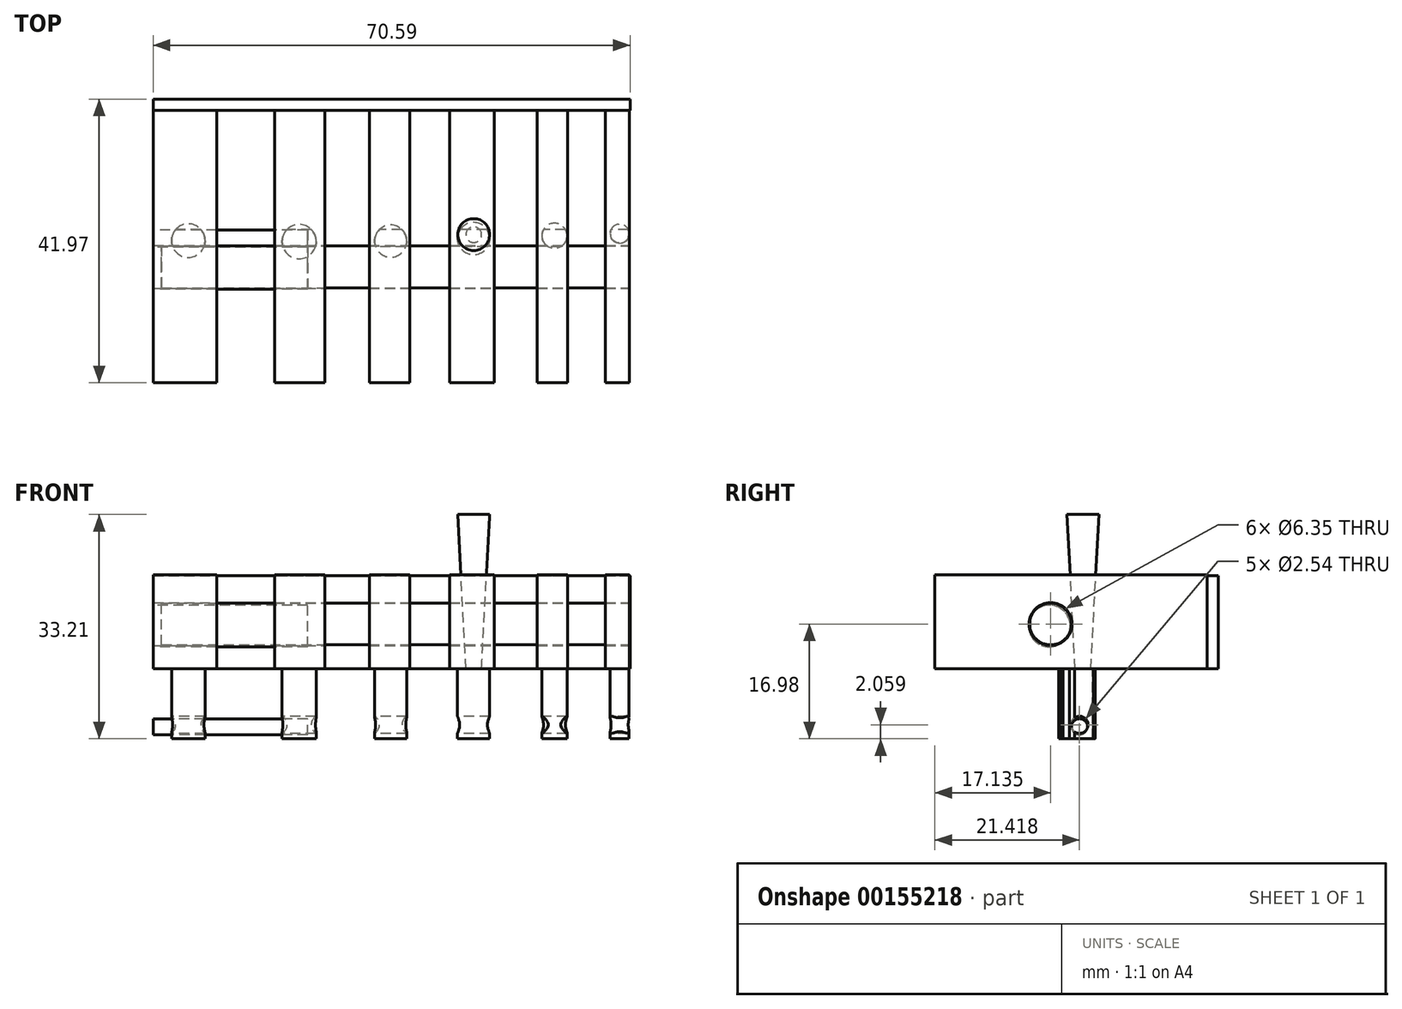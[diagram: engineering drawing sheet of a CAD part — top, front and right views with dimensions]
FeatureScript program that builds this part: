
annotation { "Feature Type Name" : "Feature", "Feature Type Description" : "" }
export const myFeature = defineFeature(function(context is Context, id is Id, definition is map)
    precondition{}
    {
        {
            var Q0;
            Q0=qCreatedBy(makeId("Front.planeOp"),FACE);
            var sketch = newSketch(context, id + "F0", { "sketchPlane" : qUnion([Q0])});
            skLineSegment(sketch, "E0.bottom", {"start": v(0, 0) * mm, "end": v(9.39, 0) * mm});
            skLineSegment(sketch, "E0.top", {"start": v(0, 13.9) * mm, "end": v(9.39, 13.9) * mm});
            skLineSegment(sketch, "E0.left", {"start": v(0, 0) * mm, "end": v(0, 13.9) * mm});
            skLineSegment(sketch, "E1.left", {"start": v(0, 13.9) * mm, "end": v(0, 0) * mm});
            skLineSegment(sketch, "E1.right", {"start": v(9.39, 13.9) * mm, "end": v(9.39, 0) * mm});
            skLineSegment(sketch, "E2.bottom", {"start": v(17.95, 13.9) * mm, "end": v(25.38, 13.9) * mm});
            skLineSegment(sketch, "E2.top", {"start": v(17.95, 0) * mm, "end": v(25.38, 0) * mm});
            skLineSegment(sketch, "E2.left", {"start": v(17.95, 13.9) * mm, "end": v(17.95, 0) * mm});
            skLineSegment(sketch, "E2.right", {"start": v(25.38, 13.9) * mm, "end": v(25.38, 0) * mm});
            skLineSegment(sketch, "E3.bottom", {"start": v(37.97, 13.9) * mm, "end": v(32, 13.9) * mm});
            skLineSegment(sketch, "E3.top", {"start": v(37.97, 0) * mm, "end": v(32, 0) * mm});
            skLineSegment(sketch, "E3.left", {"start": v(37.97, 13.9) * mm, "end": v(37.97, 0) * mm});
            skLineSegment(sketch, "E3.right", {"start": v(32, 13.9) * mm, "end": v(32, 0) * mm});
            skLineSegment(sketch, "E4.bottom", {"start": v(50.49, 13.9) * mm, "end": v(43.88, 13.9) * mm});
            skLineSegment(sketch, "E4.top", {"start": v(50.49, 0) * mm, "end": v(43.88, 0) * mm});
            skLineSegment(sketch, "E4.left", {"start": v(50.49, 13.9) * mm, "end": v(50.49, 0) * mm});
            skLineSegment(sketch, "E4.right", {"start": v(43.88, 13.9) * mm, "end": v(43.88, 0) * mm});
            skLineSegment(sketch, "E5.bottom", {"start": v(56.83, 13.9) * mm, "end": v(61.35, 13.9) * mm});
            skLineSegment(sketch, "E5.top", {"start": v(56.83, 0) * mm, "end": v(61.35, 0) * mm});
            skLineSegment(sketch, "E5.left", {"start": v(56.83, 13.9) * mm, "end": v(56.83, 0) * mm});
            skLineSegment(sketch, "E5.right", {"start": v(61.35, 13.9) * mm, "end": v(61.35, 0) * mm});
            skLineSegment(sketch, "E6.bottom", {"start": v(66.92, 13.9) * mm, "end": v(70.51, 13.9) * mm});
            skLineSegment(sketch, "E6.top", {"start": v(66.92, 0) * mm, "end": v(70.51, 0) * mm});
            skLineSegment(sketch, "E6.left", {"start": v(66.92, 13.9) * mm, "end": v(66.92, 0) * mm});
            skLineSegment(sketch, "E6.right", {"start": v(70.51, 13.9) * mm, "end": v(70.51, 0) * mm});
            skPoint(sketch, "E7.orphan", {"position": v(75.93, 13.9) * mm});
            skLineSegment(sketch, "E8.trimOffspring", {"start": v(43.88, 0) * mm, "end": v(50.49, 0) * mm});
            skLineSegment(sketch, "E9.trimOffspring", {"start": v(43.88, 13.9) * mm, "end": v(50.49, 13.9) * mm});
            skLineSegment(sketch, "E10.trimOffspring", {"start": v(32, 13.9) * mm, "end": v(37.97, 13.9) * mm});
            skLineSegment(sketch, "E11.trimOffspring", {"start": v(32, 0) * mm, "end": v(37.97, 0) * mm});
            skSolve(sketch);
        }
        {
            var Q0;
            Q0 = qSketchRegion(id + "F0", true);
            extrude(context, id + "F1", {"entities" : qUnion([Q0]), "depth" : 0.04 * yard});
        }
        {
            var Q0;
            Q0=makeQuery(id+"F1.opExtrude","SWEPT_FACE",FACE,{"disambiguationData":[OSD([sQuery(id+"F0.wireOp",EDGE,"E6.right")])]});
            var sketch = newSketch(context, id + "F2", { "sketchPlane" : qUnion([Q0])});
            skPoint(sketch, "E12", {"position": v(-23.18, 6.63) * mm});
            skSolve(sketch);
        }
        {
            var Q0;
            Q0=sQuery(id+"F2.wireOp",VERTEX,"E12");
            var Q1;
            Q1=makeQuery(id+"F1.opExtrude","SWEPT_BODY",BODY,{"disambiguationData":[OSD([sQuery(id+"F0.wireOp",EDGE,"E0.top"),sQuery(id+"F0.wireOp",EDGE,"E0.bottom"),sQuery(id+"F0.wireOp",EDGE,"E1.left"),sQuery(id+"F0.wireOp",EDGE,"E1.right")])]});
            var Q2;
            Q2=makeQuery(id+"F1.opExtrude","SWEPT_BODY",BODY,{"disambiguationData":[OSD([sQuery(id+"F0.wireOp",EDGE,"E2.left"),sQuery(id+"F0.wireOp",EDGE,"E2.right"),sQuery(id+"F0.wireOp",EDGE,"E2.bottom"),sQuery(id+"F0.wireOp",EDGE,"E2.top")])]});
            var Q3;
            Q3=makeQuery(id+"F1.opExtrude","SWEPT_BODY",BODY,{"disambiguationData":[OSD([sQuery(id+"F0.wireOp",EDGE,"E3.left"),sQuery(id+"F0.wireOp",EDGE,"E3.right"),sQuery(id+"F0.wireOp",EDGE,"E10.trimOffspring"),sQuery(id+"F0.wireOp",EDGE,"E11.trimOffspring")])]});
            var Q4;
            Q4=makeQuery(id+"F1.opExtrude","SWEPT_BODY",BODY,{"disambiguationData":[OSD([sQuery(id+"F0.wireOp",EDGE,"E4.left"),sQuery(id+"F0.wireOp",EDGE,"E4.right"),sQuery(id+"F0.wireOp",EDGE,"E8.trimOffspring"),sQuery(id+"F0.wireOp",EDGE,"E9.trimOffspring")])]});
            var Q5;
            Q5=makeQuery(id+"F1.opExtrude","SWEPT_BODY",BODY,{"disambiguationData":[OSD([sQuery(id+"F0.wireOp",EDGE,"E5.left"),sQuery(id+"F0.wireOp",EDGE,"E5.right"),sQuery(id+"F0.wireOp",EDGE,"E5.top"),sQuery(id+"F0.wireOp",EDGE,"E5.bottom")])]});
            var Q6;
            Q6=makeQuery(id+"F1.opExtrude","SWEPT_BODY",BODY,{"disambiguationData":[OSD([sQuery(id+"F0.wireOp",EDGE,"E6.left"),sQuery(id+"F0.wireOp",EDGE,"E6.right"),sQuery(id+"F0.wireOp",EDGE,"E6.bottom"),sQuery(id+"F0.wireOp",EDGE,"E6.top")])]});
            hole(context, id + "F3", {"style" : HoleStyle.SIMPLE, "endStyle" : HoleEndStyle.THROUGH, "holeDiameter" : 6.35 * mm, "locations" : qUnion([Q0]), "scope" : qUnion([Q1, Q2, Q3, Q4, Q5, Q6]), "isTappedThrough" : true});
        }
        {
            var Q0;
            Q0=makeQuery(id+"F1.opExtrude","SWEPT_FACE",FACE,{"disambiguationData":[OSD([sQuery(id+"F0.wireOp",EDGE,"E6.right")])]});
            var sketch = newSketch(context, id + "F4", { "sketchPlane" : qUnion([Q0])});
            skCircle(sketch, "E13", {"center": v(-23.18, 6.63) * mm, "radius": 3.1 * mm});
            skSolve(sketch);
        }
        {
            var Q0;
            Q0 = qSketchRegion(id + "F4", true);
            extrude(context, id + "F5", {"entities" : qUnion([Q0]), "oppositeDirection" : true, "depth" : 0.08 * yard});
        }
        {
            var Q0;
            Q0=qCreatedBy(makeId("Front.planeOp"),FACE);
            var sketch = newSketch(context, id + "F6", { "sketchPlane" : qUnion([Q0])});
            skLineSegment(sketch, "E14.bottom", {"start": v(0, 13.78) * mm, "end": v(70.6, 13.78) * mm});
            skLineSegment(sketch, "E14.top", {"start": v(0, 0) * mm, "end": v(70.6, 0) * mm});
            skLineSegment(sketch, "E14.left", {"start": v(0, 13.78) * mm, "end": v(0, 0) * mm});
            skLineSegment(sketch, "E14.right", {"start": v(70.6, 13.78) * mm, "end": v(70.6, 0) * mm});
            skSolve(sketch);
        }
        {
            var Q0;
            Q0 = qSketchRegion(id + "F6", true);
            extrude(context, id + "F7", {"entities" : qUnion([Q0]), "oppositeDirection" : true, "depth" : 0 * yard});
        }
        {
            var Q0;
            Q0=qCreatedBy(makeId("Top.planeOp"),FACE);
            var sketch = newSketch(context, id + "F8", { "sketchPlane" : qUnion([Q0])});
            skCircle(sketch, "E15", {"center": v(5.19, -19.27) * mm, "radius": 2.48 * mm});
            skCircle(sketch, "E16", {"center": v(21.6, -19.41) * mm, "radius": 2.53 * mm});
            skCircle(sketch, "E17", {"center": v(35.15, -19.34) * mm, "radius": 2.38 * mm});
            skCircle(sketch, "E18", {"center": v(47.42, -18.96) * mm, "radius": 2.38 * mm});
            skCircle(sketch, "E19", {"center": v(59.4, -18.55) * mm, "radius": 1.86 * mm});
            skCircle(sketch, "E20", {"center": v(69.05, -18.24) * mm, "radius": 1.4 * mm});
            skSolve(sketch);
        }
        {
            var Q0;
            Q0 = qSketchRegion(id + "F8", true);
            extrude(context, id + "F9", {"entities" : qUnion([Q0]), "oppositeDirection" : true, "depth" : 0.01 * yard});
        }
        {
            var Q0;
            Q0=qCreatedBy(makeId("Top.planeOp"),FACE);
            var sketch = newSketch(context, id + "F10", { "sketchPlane" : qUnion([Q0])});
            skLineSegment(sketch, "E21", {"start": v(5.2, -20.14) * mm, "end": v(22.3, -20.14) * mm});
            skLineSegment(sketch, "E22", {"start": v(22.3, -20.14) * mm, "end": v(35.52, -20.14) * mm});
            skLineSegment(sketch, "E23", {"start": v(35.52, -20.14) * mm, "end": v(47.05, -20.14) * mm});
            skLineSegment(sketch, "E24", {"start": v(47.05, -20.14) * mm, "end": v(59.35, -20.14) * mm});
            skLineSegment(sketch, "E25", {"start": v(59.35, -20.14) * mm, "end": v(69.43, -18.4) * mm});
            skLineSegment(sketch, "E26", {"start": v(5.2, -20.14) * mm, "end": v(7.22, -20.14) * mm});
            skLineSegment(sketch, "E27.bottom", {"start": v(5.2, -20.14) * mm, "end": v(35.52, -20.14) * mm});
            skLineSegment(sketch, "E27.top", {"start": v(5.2, -17.8) * mm, "end": v(35.52, -17.8) * mm});
            skLineSegment(sketch, "E27.left", {"start": v(5.2, -20.14) * mm, "end": v(5.2, -17.8) * mm});
            skLineSegment(sketch, "E27.right", {"start": v(35.52, -20.14) * mm, "end": v(35.52, -17.8) * mm});
            skSolve(sketch);
        }
        {
            var Q0;
            Q0=qCreatedBy(makeId("Right.planeOp"),FACE);
            var sketch = newSketch(context, id + "F11", { "sketchPlane" : qUnion([Q0])});
            skPoint(sketch, "E28", {"position": v(-18.9, -8.3) * mm});
            skSolve(sketch);
        }
        {
            var Q0;
            Q0=sQuery(id+"F11.wireOp",VERTEX,"E28");
            var Q1;
            Q1=makeQuery(id+"F9.opExtrude","SWEPT_BODY",BODY,{"disambiguationData":[OSD([sQuery(id+"F8.wireOp",EDGE,"E15")])]});
            var Q2;
            Q2=makeQuery(id+"F9.opExtrude","SWEPT_BODY",BODY,{"disambiguationData":[OSD([sQuery(id+"F8.wireOp",EDGE,"E16")])]});
            var Q3;
            Q3=makeQuery(id+"F9.opExtrude","SWEPT_BODY",BODY,{"disambiguationData":[OSD([sQuery(id+"F8.wireOp",EDGE,"E17")])]});
            var Q4;
            Q4=makeQuery(id+"F9.opExtrude","SWEPT_BODY",BODY,{"disambiguationData":[OSD([sQuery(id+"F8.wireOp",EDGE,"E18")])]});
            var Q5;
            Q5=makeQuery(id+"F9.opExtrude","SWEPT_BODY",BODY,{"disambiguationData":[OSD([sQuery(id+"F8.wireOp",EDGE,"E19")])]});
            var Q6;
            Q6=makeQuery(id+"F9.opExtrude","SWEPT_BODY",BODY,{"disambiguationData":[OSD([sQuery(id+"F8.wireOp",EDGE,"E20")])]});
            hole(context, id + "F12", {"style" : HoleStyle.SIMPLE, "endStyle" : HoleEndStyle.THROUGH, "oppositeDirection" : true, "holeDiameter" : 2.54 * mm, "locations" : qUnion([Q0]), "scope" : qUnion([Q1, Q2, Q3, Q4, Q5, Q6]), "isTappedThrough" : true});
        }
        {
            var Q0;
            Q0=qCreatedBy(makeId("Right.planeOp"),FACE);
            var sketch = newSketch(context, id + "F13", { "sketchPlane" : qUnion([Q0])});
            skCircle(sketch, "E29", {"center": v(-18.9, -8.58) * mm, "radius": 1.2 * mm});
            skSolve(sketch);
        }
        {
            var Q0;
            Q0 = qSketchRegion(id + "F13", true);
            extrude(context, id + "F14", {"entities" : qUnion([Q0]), "depth" : 0.03 * yard});
        }
        {
            var Q0;
            Q0=qCreatedBy(makeId("Right.planeOp"),FACE);
            var sketch = newSketch(context, id + "F15", { "sketchPlane" : qUnion([Q0])});
            skCircle(sketch, "E30", {"center": v(-23.35, 6.34) * mm, "radius": 3.08 * mm});
            skSolve(sketch);
        }
        {
            var Q0;
            Q0 = qSketchRegion(id + "F15", true);
            extrude(context, id + "F16", {"entities" : qUnion([Q0]), "depth" : 0.03 * yard});
        }
        {
            var Q0;
            Q0=qCreatedBy(makeId("Top.planeOp"),FACE);
            var sketch = newSketch(context, id + "F17", { "sketchPlane" : qUnion([Q0])});
            skCircle(sketch, "E31", {"center": v(47.44, -18.38) * mm, "radius": 1.16 * mm});
            skSolve(sketch);
        }
        {
            var Q0;
            Q0 = qSketchRegion(id + "F17", true);
            extrude(context, id + "F18", {"entities" : qUnion([Q0]), "depth" : 0.03 * yard, "hasDraft" : true, "draftAngle" : 3 * degree});
        }
        {
            var Q0;
            Q0=makeQuery(id+"F9.opExtrude","CAP_FACE",FACE,{"disambiguationData":[OSD([sQuery(id+"F8.wireOp",EDGE,"E16")])],"isStart":false});
            var sketch = newSketch(context, id + "F19", { "sketchPlane" : qUnion([Q0])});
            skCircle(sketch, "E32", {"center": v(21.6, 19.41) * mm, "radius": 1.08 * mm});
            skSolve(sketch);
        }
        {
            var Q0;
            Q0=sQuery(id+"F19.wireOp",EDGE,"E32");
            var Q1;
            Q1=sQuery(id+"F10.wireOp",EDGE,"E27.bottom");
            extrude(context, id + "F20", {"bodyType" : ToolBodyType.SURFACE, "surfaceEntities" : qUnion([Q0, Q1]), "depth" : 0.03 * yard});
        }
    });
